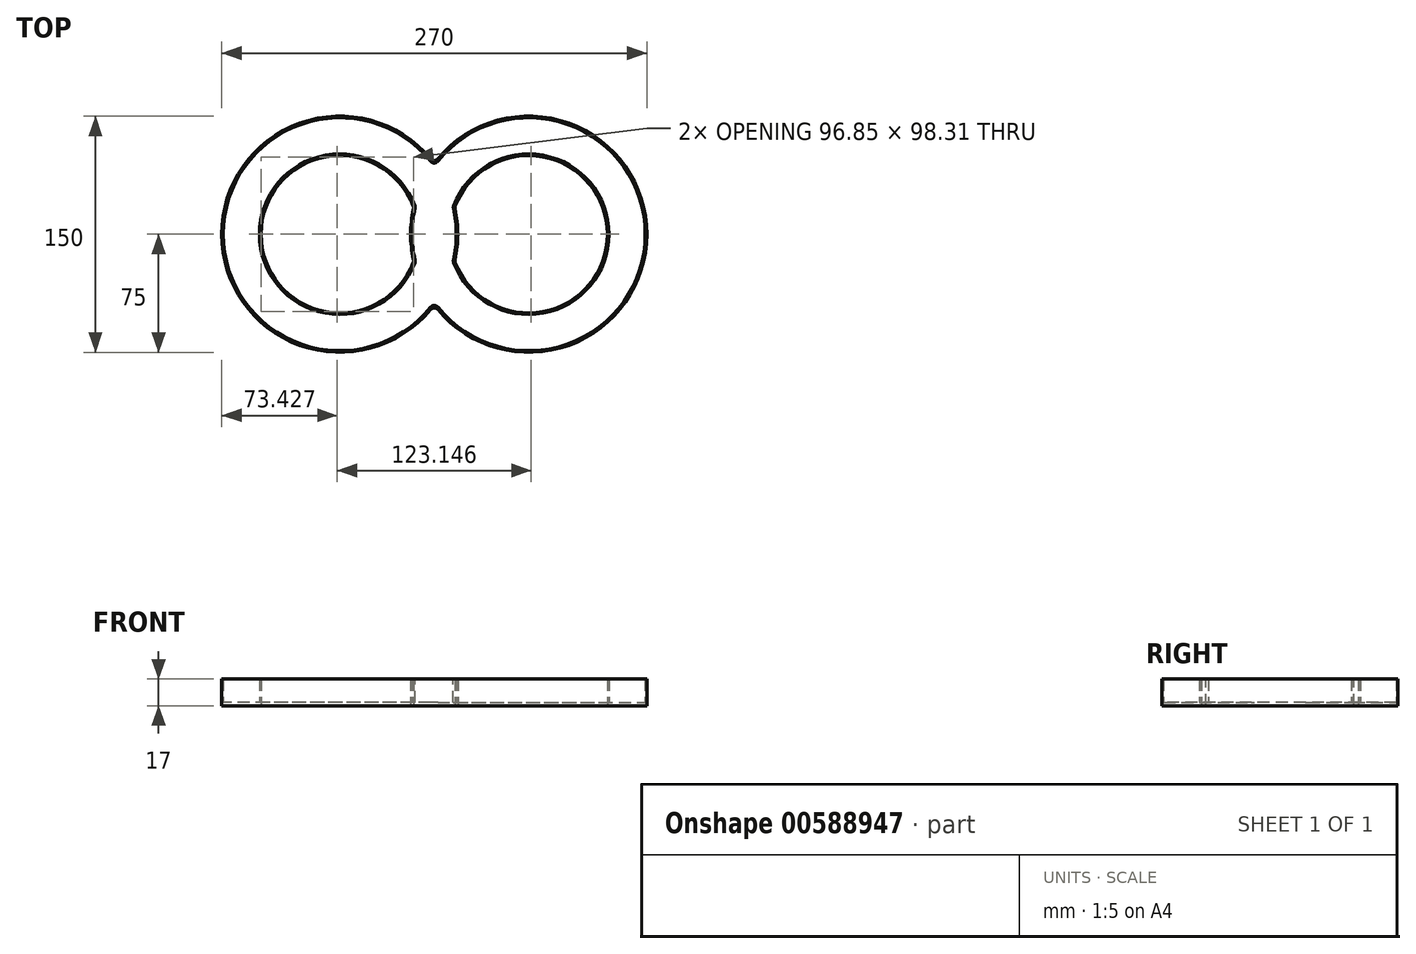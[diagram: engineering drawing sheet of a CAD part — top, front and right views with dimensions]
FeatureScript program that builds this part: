
annotation { "Feature Type Name" : "Feature", "Feature Type Description" : "" }
export const myFeature = defineFeature(function(context is Context, id is Id, definition is map)
    precondition{}
    {
        {
            var Q0;
            Q0=qCreatedBy(makeId("Top.planeOp"),FACE);
            var sketch = newSketch(context, id + "F0", { "sketchPlane" : qUnion([Q0])});
            skCircle(sketch, "E0", {"center": v(0, 0) * mm, "radius": 62.5 * mm, "construction": true});
            skLineSegment(sketch, "E1", {"start": v(0, 0) * mm, "end": v(120, 0) * mm, "construction": true});
            skCircle(sketch, "E2", {"center": v(120, 0) * mm, "radius": 62.5 * mm, "construction": true});
            skCircle(sketch, "E3", {"center": v(0, 0) * mm, "radius": 50 * mm});
            skCircle(sketch, "E4", {"center": v(120, 0) * mm, "radius": 50 * mm});
            skCircle(sketch, "E5", {"center": v(0, 0) * mm, "radius": 75 * mm});
            skCircle(sketch, "E6", {"center": v(120, 0) * mm, "radius": 75 * mm});
            skLineSegment(sketch, "E7", {"start": v(0, 0) * mm, "end": v(-75, 0) * mm, "construction": true});
            skLineSegment(sketch, "E8", {"start": v(120, 0) * mm, "end": v(195, 0) * mm, "construction": true});
            skSolve(sketch);
        }
        {
            var Q0;
            Q0 = qSketchRegion(id + "F0", true);
            var Q1;
            {var subQ0=sQuery(id+"F0.wireOp",EDGE,"E6");var subQ1=sQuery(id+"F0.wireOp",EDGE,"E3");var subQ2=makeQuery(id+"F0.imprint","INTERSECT",VERTEX,{"disambiguationData":[OD(0.0)],"derivedFrom":[subQ1,subQ0]});Q1=makeQuery(id+"F0.imprint","IMPRINT",FACE,{"disambiguationData":[TD([[makeQuery(id+"F0.imprint","IMPRINT",EDGE,{"disambiguationData":[TD([[subQ2,1.0]])],"derivedFrom":subQ1}),1.0]])]});}
            var Q2;
            {var subQ0=sQuery(id+"F0.wireOp",EDGE,"E5");var subQ1=sQuery(id+"F0.wireOp",EDGE,"E4");var subQ2=makeQuery(id+"F0.imprint","INTERSECT",VERTEX,{"disambiguationData":[OD(0.0)],"derivedFrom":[subQ1,subQ0]});Q2=makeQuery(id+"F0.imprint","IMPRINT",FACE,{"disambiguationData":[TD([[makeQuery(id+"F0.imprint","IMPRINT",EDGE,{"disambiguationData":[TD([[subQ2,-1.0]])],"derivedFrom":subQ1}),1.0]])]});}
            extrude(context, id + "F1", {"entities" : qUnion([Q0, Q1, Q2]), "depth" : 2 * mm, "offsetDistance" : 25 * mm});
        }
        {
            var Q0;
            Q0=makeQuery(id+"F1.opExtrude","CAP_FACE",FACE,{"disambiguationData":[OSD([sQuery(id+"F0.wireOp",EDGE,"E3"),sQuery(id+"F0.wireOp",EDGE,"E4"),sQuery(id+"F0.wireOp",EDGE,"E5"),sQuery(id+"F0.wireOp",EDGE,"E6")])],"isStart":false});
            var sketch = newSketch(context, id + "F2", { "sketchPlane" : qUnion([Q0])});
            skArc(sketch, "E9.0.0", {"start": v(60, -45) * mm, "mid": v(195, 0) * mm, "end": v(60, 45) * mm});
            skArc(sketch, "E9.0.1", {"start": v(60, 45) * mm, "mid": v(-75, 0) * mm, "end": v(60, -45) * mm});
            skArc(sketch, "E10.0", {"start": v(46.98, 17.12) * mm, "mid": v(45, 0) * mm, "end": v(46.98, -17.12) * mm});
            skArc(sketch, "E11.0", {"start": v(46.98, 17.12) * mm, "mid": v(-50, 0) * mm, "end": v(46.98, -17.12) * mm});
            skArc(sketch, "E12.0", {"start": v(73.02, -17.12) * mm, "mid": v(170, 0) * mm, "end": v(73.02, 17.12) * mm});
            skArc(sketch, "E13.0", {"start": v(73.02, -17.12) * mm, "mid": v(75, 0) * mm, "end": v(73.02, 17.12) * mm});
            skArc(sketch, "E14", {"start": v(60, 43.31) * mm, "mid": v(-74, 0) * mm, "end": v(60, -43.31) * mm});
            skArc(sketch, "E15", {"start": v(48.02, 17.18) * mm, "mid": v(46, 0) * mm, "end": v(48.02, -17.18) * mm});
            skArc(sketch, "E16", {"start": v(48.02, 17.18) * mm, "mid": v(-51, 0) * mm, "end": v(48.02, -17.18) * mm});
            skArc(sketch, "E17", {"start": v(71.98, -17.18) * mm, "mid": v(171, 0) * mm, "end": v(71.98, 17.18) * mm});
            skArc(sketch, "E18.trimOffspring", {"start": v(60, -43.31) * mm, "mid": v(194, 0) * mm, "end": v(60, 43.31) * mm});
            skArc(sketch, "E19.trimOffspring", {"start": v(71.98, -17.18) * mm, "mid": v(74, 0) * mm, "end": v(71.98, 17.18) * mm});
            skSolve(sketch);
        }
        {
            var Q0;
            Q0 = qSketchRegion(id + "F2", true);
            var Q1;
            Q1=makeQuery(id+"F2.imprint","IMPRINT",FACE,{"disambiguationData":[TD([[makeQuery(id+"F2.imprint","IMPRINT",EDGE,{"derivedFrom":sQuery(id+"F2.wireOp",EDGE,"E10.0")}),1.0]])]});
            var Q2;
            Q2=makeQuery(id+"F2.imprint","IMPRINT",FACE,{"disambiguationData":[TD([[makeQuery(id+"F2.imprint","IMPRINT",EDGE,{"derivedFrom":sQuery(id+"F2.wireOp",EDGE,"E12.0")}),-1.0]])]});
            extrude(context, id + "F3", {"entities" : qUnion([Q0, Q1, Q2]), "operationType" : NewBodyOperationType.ADD, "depth" : 15 * mm, "offsetDistance" : 25 * mm});
        }
        {
            var Q0;
            {var subQ0=sQuery(id+"F2.wireOp",EDGE,"E9.0.1");var subQ1=sQuery(id+"F2.wireOp",EDGE,"E9.0.0");var subQ2=sQuery(id+"F0.wireOp",EDGE,"E6");var subQ3=sQuery(id+"F0.wireOp",EDGE,"E5");Q0=makeQuery(id+"F3.boolean.opBoolean","MERGE",EDGE,{"derivedFrom":[makeQuery(id+"F1.opExtrude","SWEPT_EDGE",EDGE,{"disambiguationData":[OSD([subQ3,subQ2]),TDD([makeQuery(id+"F0.imprint","INTERSECT",VERTEX,{"disambiguationData":[OD(0.0)],"derivedFrom":[subQ3,subQ2]})])]}),makeQuery(id+"F3.opExtrude","SWEPT_EDGE",EDGE,{"disambiguationData":[OSD([subQ1,subQ0]),TDD([makeQuery(id+"F2.imprint","INTERSECT",VERTEX,{"disambiguationData":[OD(0.0)],"derivedFrom":[subQ1,subQ0]})])]})]});}
            var Q1;
            {var subQ0=sQuery(id+"F2.wireOp",EDGE,"E18.trimOffspring");var subQ1=sQuery(id+"F2.wireOp",EDGE,"E14");Q1=makeQuery(id+"F3.opExtrude","SWEPT_EDGE",EDGE,{"disambiguationData":[OSD([subQ1,subQ0]),TDD([makeQuery(id+"F2.imprint","INTERSECT",VERTEX,{"disambiguationData":[OD(0.0)],"derivedFrom":[subQ1,subQ0]})])]});}
            var Q2;
            {var subQ0=sQuery(id+"F2.wireOp",EDGE,"E18.trimOffspring");var subQ1=sQuery(id+"F2.wireOp",EDGE,"E14");Q2=makeQuery(id+"F3.opExtrude","SWEPT_EDGE",EDGE,{"disambiguationData":[OSD([subQ1,subQ0]),TDD([makeQuery(id+"F2.imprint","INTERSECT",VERTEX,{"disambiguationData":[OD(1.0)],"derivedFrom":[subQ1,subQ0]})])]});}
            var Q3;
            {var subQ0=sQuery(id+"F2.wireOp",EDGE,"E9.0.1");var subQ1=sQuery(id+"F2.wireOp",EDGE,"E9.0.0");var subQ2=sQuery(id+"F0.wireOp",EDGE,"E6");var subQ3=sQuery(id+"F0.wireOp",EDGE,"E5");Q3=makeQuery(id+"F3.boolean.opBoolean","MERGE",EDGE,{"derivedFrom":[makeQuery(id+"F1.opExtrude","SWEPT_EDGE",EDGE,{"disambiguationData":[OSD([subQ3,subQ2]),TDD([makeQuery(id+"F0.imprint","INTERSECT",VERTEX,{"disambiguationData":[OD(1.0)],"derivedFrom":[subQ3,subQ2]})])]}),makeQuery(id+"F3.opExtrude","SWEPT_EDGE",EDGE,{"disambiguationData":[OSD([subQ1,subQ0]),TDD([makeQuery(id+"F2.imprint","INTERSECT",VERTEX,{"disambiguationData":[OD(1.0)],"derivedFrom":[subQ1,subQ0]})])]})]});}
            var Q4;
            {var subQ0=sQuery(id+"F2.wireOp",EDGE,"E19.trimOffspring");var subQ1=sQuery(id+"F2.wireOp",EDGE,"E17");Q4=makeQuery(id+"F3.opExtrude","SWEPT_EDGE",EDGE,{"disambiguationData":[OSD([subQ1,subQ0]),TDD([makeQuery(id+"F2.imprint","INTERSECT",VERTEX,{"disambiguationData":[OD(0.0)],"derivedFrom":[subQ1,subQ0]})])]});}
            var Q5;
            {var subQ0=sQuery(id+"F2.wireOp",EDGE,"E19.trimOffspring");var subQ1=sQuery(id+"F2.wireOp",EDGE,"E17");Q5=makeQuery(id+"F3.opExtrude","SWEPT_EDGE",EDGE,{"disambiguationData":[OSD([subQ1,subQ0]),TDD([makeQuery(id+"F2.imprint","INTERSECT",VERTEX,{"disambiguationData":[OD(1.0)],"derivedFrom":[subQ1,subQ0]})])]});}
            var Q6;
            {var subQ0=sQuery(id+"F2.wireOp",EDGE,"E13.0");var subQ1=sQuery(id+"F2.wireOp",EDGE,"E12.0");var subQ2=sQuery(id+"F0.wireOp",EDGE,"E5");var subQ3=sQuery(id+"F0.wireOp",EDGE,"E4");Q6=makeQuery(id+"F3.boolean.opBoolean","MERGE",EDGE,{"derivedFrom":[makeQuery(id+"F1.opExtrude","SWEPT_EDGE",EDGE,{"disambiguationData":[OSD([subQ3,subQ2]),TDD([makeQuery(id+"F0.imprint","INTERSECT",VERTEX,{"disambiguationData":[OD(1.0)],"derivedFrom":[subQ3,subQ2]})])]}),makeQuery(id+"F3.opExtrude","SWEPT_EDGE",EDGE,{"disambiguationData":[OSD([subQ1,subQ0]),TDD([makeQuery(id+"F2.imprint","INTERSECT",VERTEX,{"disambiguationData":[OD(1.0)],"derivedFrom":[subQ1,subQ0]})])]})]});}
            var Q7;
            {var subQ0=sQuery(id+"F2.wireOp",EDGE,"E13.0");var subQ1=sQuery(id+"F2.wireOp",EDGE,"E12.0");var subQ2=sQuery(id+"F0.wireOp",EDGE,"E5");var subQ3=sQuery(id+"F0.wireOp",EDGE,"E4");Q7=makeQuery(id+"F3.boolean.opBoolean","MERGE",EDGE,{"derivedFrom":[makeQuery(id+"F1.opExtrude","SWEPT_EDGE",EDGE,{"disambiguationData":[OSD([subQ3,subQ2]),TDD([makeQuery(id+"F0.imprint","INTERSECT",VERTEX,{"disambiguationData":[OD(0.0)],"derivedFrom":[subQ3,subQ2]})])]}),makeQuery(id+"F3.opExtrude","SWEPT_EDGE",EDGE,{"disambiguationData":[OSD([subQ1,subQ0]),TDD([makeQuery(id+"F2.imprint","INTERSECT",VERTEX,{"disambiguationData":[OD(0.0)],"derivedFrom":[subQ1,subQ0]})])]})]});}
            var Q8;
            {var subQ0=sQuery(id+"F2.wireOp",EDGE,"E16");var subQ1=sQuery(id+"F2.wireOp",EDGE,"E15");Q8=makeQuery(id+"F3.opExtrude","SWEPT_EDGE",EDGE,{"disambiguationData":[OSD([subQ1,subQ0]),TDD([makeQuery(id+"F2.imprint","INTERSECT",VERTEX,{"disambiguationData":[OD(0.0)],"derivedFrom":[subQ1,subQ0]})])]});}
            var Q9;
            {var subQ0=sQuery(id+"F2.wireOp",EDGE,"E16");var subQ1=sQuery(id+"F2.wireOp",EDGE,"E15");Q9=makeQuery(id+"F3.opExtrude","SWEPT_EDGE",EDGE,{"disambiguationData":[OSD([subQ1,subQ0]),TDD([makeQuery(id+"F2.imprint","INTERSECT",VERTEX,{"disambiguationData":[OD(1.0)],"derivedFrom":[subQ1,subQ0]})])]});}
            var Q10;
            {var subQ0=sQuery(id+"F2.wireOp",EDGE,"E11.0");var subQ1=sQuery(id+"F2.wireOp",EDGE,"E10.0");var subQ2=sQuery(id+"F0.wireOp",EDGE,"E6");var subQ3=sQuery(id+"F0.wireOp",EDGE,"E3");Q10=makeQuery(id+"F3.boolean.opBoolean","MERGE",EDGE,{"derivedFrom":[makeQuery(id+"F1.opExtrude","SWEPT_EDGE",EDGE,{"disambiguationData":[OSD([subQ3,subQ2]),TDD([makeQuery(id+"F0.imprint","INTERSECT",VERTEX,{"disambiguationData":[OD(0.0)],"derivedFrom":[subQ3,subQ2]})])]}),makeQuery(id+"F3.opExtrude","SWEPT_EDGE",EDGE,{"disambiguationData":[OSD([subQ1,subQ0]),TDD([makeQuery(id+"F2.imprint","INTERSECT",VERTEX,{"disambiguationData":[OD(0.0)],"derivedFrom":[subQ1,subQ0]})])]})]});}
            var Q11;
            {var subQ0=sQuery(id+"F2.wireOp",EDGE,"E11.0");var subQ1=sQuery(id+"F2.wireOp",EDGE,"E10.0");var subQ2=sQuery(id+"F0.wireOp",EDGE,"E6");var subQ3=sQuery(id+"F0.wireOp",EDGE,"E3");Q11=makeQuery(id+"F3.boolean.opBoolean","MERGE",EDGE,{"derivedFrom":[makeQuery(id+"F1.opExtrude","SWEPT_EDGE",EDGE,{"disambiguationData":[OSD([subQ3,subQ2]),TDD([makeQuery(id+"F0.imprint","INTERSECT",VERTEX,{"disambiguationData":[OD(1.0)],"derivedFrom":[subQ3,subQ2]})])]}),makeQuery(id+"F3.opExtrude","SWEPT_EDGE",EDGE,{"disambiguationData":[OSD([subQ1,subQ0]),TDD([makeQuery(id+"F2.imprint","INTERSECT",VERTEX,{"disambiguationData":[OD(1.0)],"derivedFrom":[subQ1,subQ0]})])]})]});}
            fillet(context, id + "F4", {"entities" : qUnion([Q0, Q1, Q2, Q3, Q4, Q5, Q6, Q7, Q8, Q9, Q10, Q11]), "radius" : 3 * mm, "tangentPropagation" : true, "allowEdgeOverflow" : false});
        }
    });
